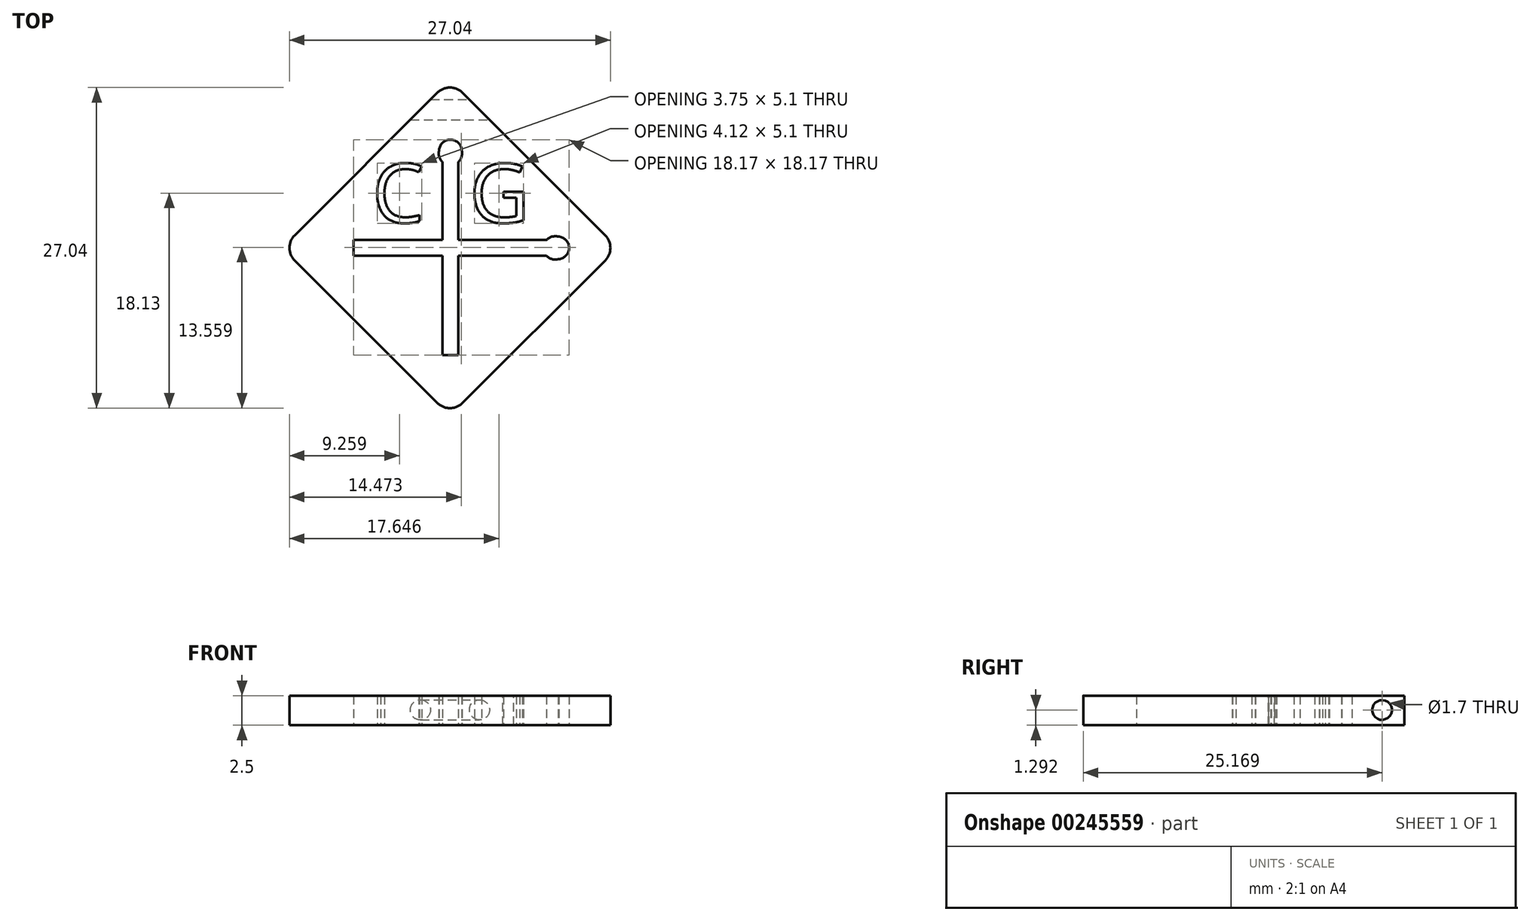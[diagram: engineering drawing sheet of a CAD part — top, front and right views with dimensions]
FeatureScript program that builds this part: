
annotation { "Feature Type Name" : "Feature", "Feature Type Description" : "" }
export const myFeature = defineFeature(function(context is Context, id is Id, definition is map)
    precondition{}
    {
        {
            var Q0;
            Q0=qCreatedBy(makeId("Top.planeOp"),FACE);
            var sketch = newSketch(context, id + "F0", { "sketchPlane" : qUnion([Q0])});
            skLineSegment(sketch, "E0", {"start": v(1.06, -1.06) * mm, "end": v(13.08, -13.08) * mm});
            skLineSegment(sketch, "E1", {"start": v(13.08, -15.2) * mm, "end": v(1.06, -27.22) * mm});
            skLineSegment(sketch, "E2", {"start": v(-1.06, -27.22) * mm, "end": v(-13.08, -15.2) * mm});
            skLineSegment(sketch, "E3", {"start": v(-13.08, -13.08) * mm, "end": v(-1.06, -1.06) * mm});
            skPoint(sketch, "E4.visualSharp", {"position": v(0, 0) * mm});
            skArc(sketch, "E4.filletArc", {"start": v(1.06, -1.06) * mm, "mid": v(0, -0.62) * mm, "end": v(-1.06, -1.06) * mm});
            skPoint(sketch, "E5.visualSharp", {"position": v(-14.14, -14.14) * mm});
            skArc(sketch, "E5.filletArc", {"start": v(-13.08, -13.08) * mm, "mid": v(-13.52, -14.14) * mm, "end": v(-13.08, -15.2) * mm});
            skPoint(sketch, "E6.visualSharp", {"position": v(14.14, -14.14) * mm});
            skArc(sketch, "E6.filletArc", {"start": v(13.08, -15.2) * mm, "mid": v(13.52, -14.14) * mm, "end": v(13.08, -13.08) * mm});
            skPoint(sketch, "E7.visualSharp", {"position": v(0, -28.28) * mm});
            skArc(sketch, "E7.filletArc", {"start": v(-1.06, -27.22) * mm, "mid": v(0, -27.66) * mm, "end": v(1.06, -27.22) * mm});
            skLineSegment(sketch, "E8", {"start": v(0, 0) * mm, "end": v(0, -31.86) * mm, "construction": true});
            skLineSegment(sketch, "E9", {"start": v(-14.14, -14.14) * mm, "end": v(14.14, -14.14) * mm, "construction": true});
            skLineSegment(sketch, "E10", {"start": v(-8.13, -13.48) * mm, "end": v(-8.13, -14.8) * mm});
            skLineSegment(sketch, "E11", {"start": v(-8.13, -14.8) * mm, "end": v(8.13, -14.8) * mm});
            skLineSegment(sketch, "E12", {"start": v(8.13, -13.48) * mm, "end": v(-8.13, -13.48) * mm});
            skLineSegment(sketch, "E13", {"start": v(-8.13, -13.48) * mm, "end": v(0, -13.48) * mm, "construction": true});
            skLineSegment(sketch, "E14", {"start": v(0, -13.48) * mm, "end": v(8.13, -13.48) * mm, "construction": true});
            skArc(sketch, "E15", {"start": v(9.18, -15.1) * mm, "mid": v(10.04, -14.12) * mm, "end": v(9.13, -13.2) * mm});
            skArc(sketch, "E16", {"start": v(9.13, -13.2) * mm, "mid": v(8.6, -13.2) * mm, "end": v(8.13, -13.48) * mm});
            skArc(sketch, "E17", {"start": v(8.13, -14.8) * mm, "mid": v(8.61, -15.1) * mm, "end": v(9.18, -15.1) * mm});
            skLineSegment(sketch, "E18", {"start": v(-0.62, -23.19) * mm, "end": v(0.7, -23.19) * mm});
            skLineSegment(sketch, "E19", {"start": v(0.7, -23.19) * mm, "end": v(0.7, -6.92) * mm});
            skLineSegment(sketch, "E20", {"start": v(-0.62, -6.92) * mm, "end": v(-0.62, -23.19) * mm});
            skLineSegment(sketch, "E21", {"start": v(-0.62, -23.19) * mm, "end": v(-0.62, -15.05) * mm, "construction": true});
            skLineSegment(sketch, "E22", {"start": v(-0.62, -15.05) * mm, "end": v(-0.62, -6.92) * mm, "construction": true});
            skArc(sketch, "E23", {"start": v(0.99, -5.88) * mm, "mid": v(0.02, -5.01) * mm, "end": v(-0.91, -5.92) * mm});
            skArc(sketch, "E24", {"start": v(-0.91, -5.92) * mm, "mid": v(-0.9, -6.46) * mm, "end": v(-0.62, -6.92) * mm});
            skArc(sketch, "E25", {"start": v(0.7, -6.92) * mm, "mid": v(1, -6.44) * mm, "end": v(0.99, -5.88) * mm});
            skText(sketch, "E26", { "text": "C\n", "fontName": "OpenSans-Regular.ttf"});
            skText(sketch, "E27", { "text": "G", "fontName": "OpenSans-Regular.ttf"});
            const initialGuessF0  = {"E26": [-0.00656, -0.01201, 1, 0, 0.005], "E27": [0.00164, -0.01201, 1, 0, 0.005]};
            skSetInitialGuess(sketch, initialGuessF0);
            skSolve(sketch);
        }
        {
            var Q0;
            Q0=makeQuery(id+"F0.imprint","IMPRINT",FACE,{"disambiguationData":[TD([[makeQuery(id+"F0.imprint","IMPRINT",EDGE,{"derivedFrom":sQuery(id+"F0.wireOp",EDGE,"E0")}),-1.0]])]});
            extrude(context, id + "F1", {"entities" : qUnion([Q0]), "depth" : 2.5 * mm});
        }
        {
            var Q0;
            Q0=qCreatedBy(makeId("Right.planeOp"),FACE);
            var sketch = newSketch(context, id + "F2", { "sketchPlane" : qUnion([Q0])});
            skCircle(sketch, "E28", {"center": v(-2.5, 1.3) * mm, "radius": 0.85 * mm});
            skSolve(sketch);
        }
        {
            var Q0;
            Q0=qSketchRegion(id+"F2",true);
            extrude(context, id + "F3", {"entities" : qUnion([Q0]), "operationType" : NewBodyOperationType.REMOVE, "endBound" : BoundingType.SYMMETRIC, "oppositeDirection" : true, "depth" : 25 * mm});
        }
    });
